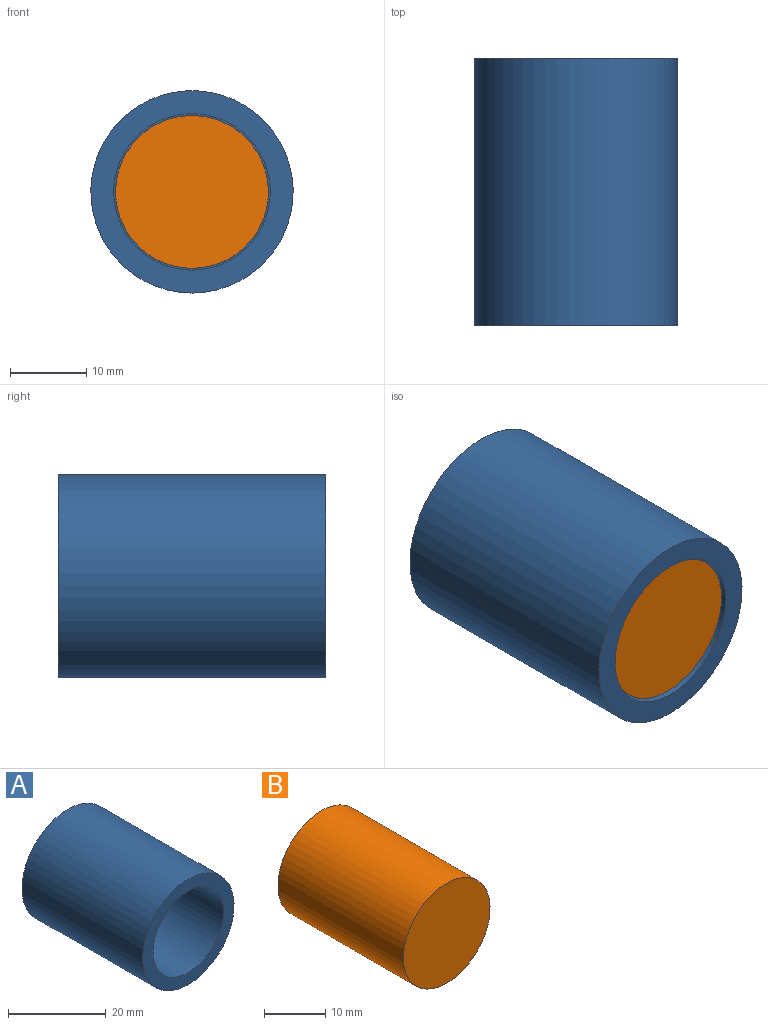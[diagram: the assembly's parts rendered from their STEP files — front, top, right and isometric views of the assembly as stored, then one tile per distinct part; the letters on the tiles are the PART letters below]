
ASSEMBLY  parts=2 mates=1
PART A: 9 faces, bbox 26.5x35x26.5 mm
  f0: plane 20.5x20.5mm, normal (0,-1,0), area 232.1mm2, adj f4,f5,f6,f7,f8
  f1: cylinder r=13.25mm len=35mm, axis (0,1,0), area 2913.8mm2, adj f2,f3
  f2: plane 26.5x26.5mm, normal (0,-1,0), area 221.5mm2, adj f1,f4
  f3: plane 26.5x26.5mm, normal (0,1,0), area 453.5mm2, adj f1,f5,f6,f7,f8
  f4: cylinder r=10.25mm len=33mm, axis (0,-1,0), area 2125.3mm2, adj f0,f2
  f5: plane 14x2mm, normal (0,0,-1), area 28mm2, adj f0,f3,f6,f7
  f6: plane 7x2mm, normal (-1,0,0), area 14mm2, adj f0,f3,f5,f8
  f7: plane 7x2mm, normal (1,0,0), area 14mm2, adj f0,f3,f5,f8
  f8: plane 14x2mm, normal (0,0,1), area 28mm2, adj f0,f3,f6,f7
PART B: 3 faces, bbox 20x29x20 mm
  f0: cylinder r=10mm len=29mm, axis (0,1,0), area 1822.1mm2, adj f1,f2
  f1: plane 20x20mm, normal (0,-1,0), area 314.2mm2, adj f0
  f2: plane 20x20mm, normal (0,1,0), area 314.2mm2, adj f0
PLACE A t=(3.05,0,3.35)mm
PLACE B t=(3.05,-5.46,3.35)mm
MATE cylindrical B.f0 <-> A.f4  axis (0,1,0) through (3.05,-19.96,3.35)mm
